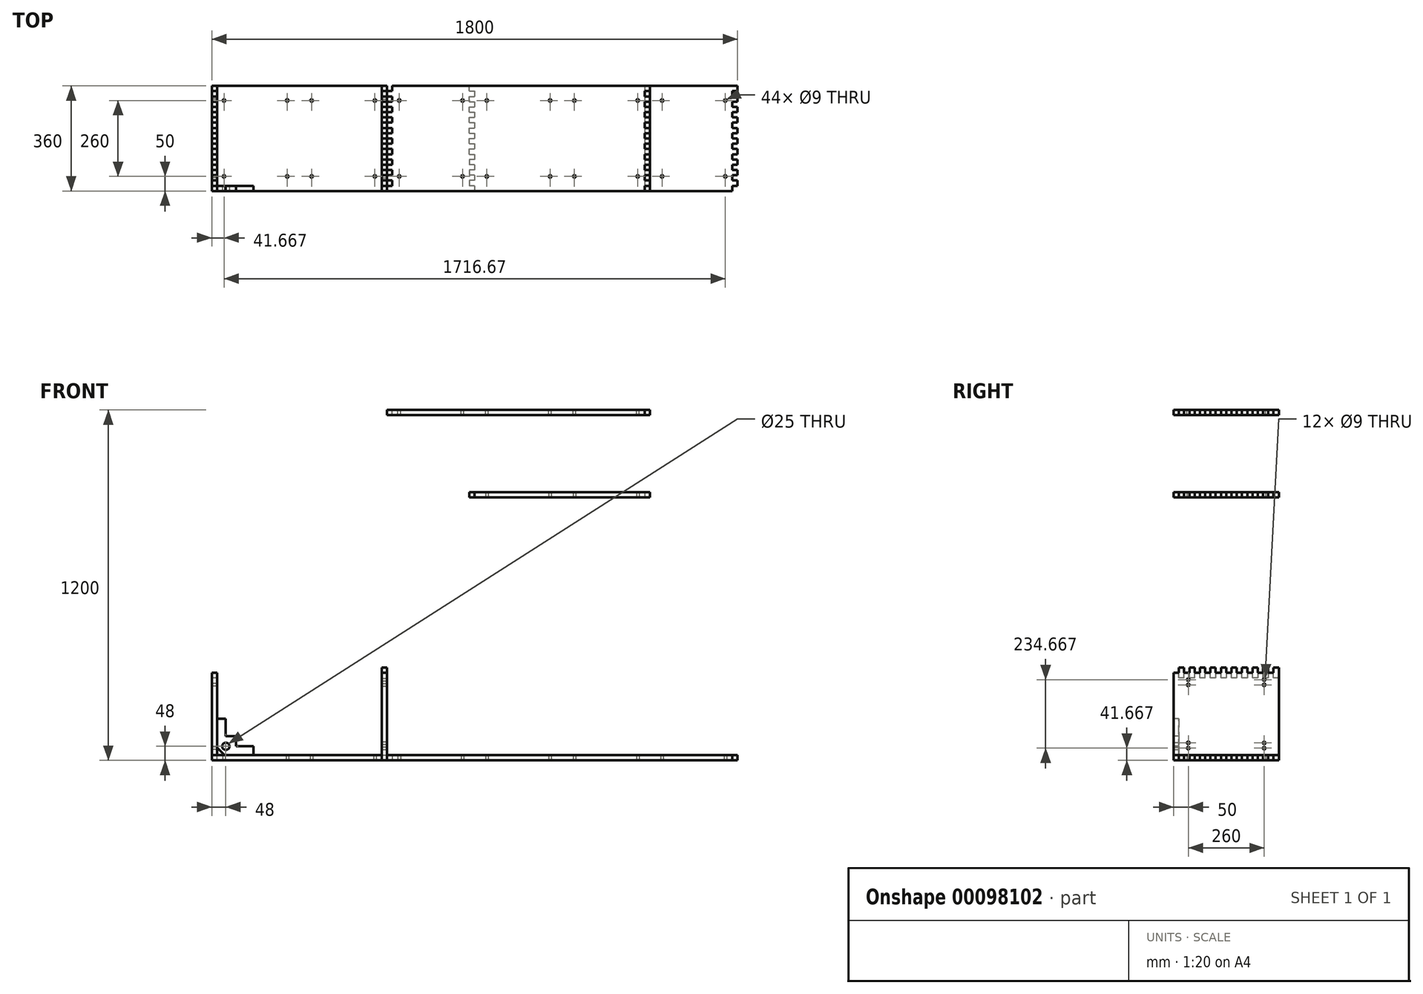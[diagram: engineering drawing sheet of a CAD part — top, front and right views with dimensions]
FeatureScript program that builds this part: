
annotation { "Feature Type Name" : "Feature", "Feature Type Description" : "" }
export const myFeature = defineFeature(function(context is Context, id is Id, definition is map)
    precondition{}
    {
        {
            var Q0;
            Q0=qCreatedBy(makeId("Right.planeOp"),FACE);
            cPlane(context, id + "F0", {"entities" : qUnion([Q0]), "cplaneType" : CPlaneType.OFFSET, "offset" : 300 * mm, "width" : 150 * mm, "height" : 150 * mm});
        }
        {
            var Q0;
            Q0=qCreatedBy(makeId("Right.planeOp"),FACE);
            cPlane(context, id + "F1", {"entities" : qUnion([Q0]), "cplaneType" : CPlaneType.OFFSET, "offset" : 600 * mm, "width" : 150 * mm, "height" : 150 * mm});
        }
        {
            var Q0;
            Q0=qCreatedBy(makeId("Right.planeOp"),FACE);
            cPlane(context, id + "F2", {"entities" : qUnion([Q0]), "cplaneType" : CPlaneType.OFFSET, "offset" : 900 * mm, "width" : 150 * mm, "height" : 150 * mm});
        }
        {
            var Q0;
            Q0=qCreatedBy(makeId("Right.planeOp"),FACE);
            cPlane(context, id + "F3", {"entities" : qUnion([Q0]), "cplaneType" : CPlaneType.OFFSET, "offset" : 1200 * mm, "width" : 150 * mm, "height" : 150 * mm});
        }
        {
            var Q0;
            Q0=qCreatedBy(makeId("Right.planeOp"),FACE);
            cPlane(context, id + "F4", {"entities" : qUnion([Q0]), "cplaneType" : CPlaneType.OFFSET, "offset" : 1500 * mm, "width" : 150 * mm, "height" : 150 * mm});
        }
        {
            var Q0;
            Q0=qCreatedBy(makeId("Right.planeOp"),FACE);
            cPlane(context, id + "F5", {"entities" : qUnion([Q0]), "cplaneType" : CPlaneType.OFFSET, "offset" : 1800 * mm, "width" : 150 * mm, "height" : 150 * mm});
        }
        {
            var Q0;
            Q0=qCreatedBy(makeId("Top.planeOp"),FACE);
            cPlane(context, id + "F6", {"entities" : qUnion([Q0]), "cplaneType" : CPlaneType.OFFSET, "offset" : 300 * mm, "width" : 150 * mm, "height" : 150 * mm});
        }
        {
            var Q0;
            Q0=qCreatedBy(makeId("Top.planeOp"),FACE);
            cPlane(context, id + "F7", {"entities" : qUnion([Q0]), "cplaneType" : CPlaneType.OFFSET, "offset" : 900 * mm, "width" : 150 * mm, "height" : 150 * mm});
        }
        {
            var Q0;
            Q0=qCreatedBy(makeId("Top.planeOp"),FACE);
            cPlane(context, id + "F8", {"entities" : qUnion([Q0]), "cplaneType" : CPlaneType.OFFSET, "offset" : 1200 * mm, "width" : 150 * mm, "height" : 150 * mm});
        }
        {
            var Q0;
            Q0=qCreatedBy(makeId("Front.planeOp"),FACE);
            cPlane(context, id + "F9", {"entities" : qUnion([Q0]), "cplaneType" : CPlaneType.OFFSET, "offset" : 360 * mm, "oppositeDirection" : true, "width" : 150 * mm, "height" : 150 * mm});
        }
        {
            var Q0;
            Q0=qCreatedBy(makeId("Top.planeOp"),FACE);
            var sketch = newSketch(context, id + "F10", { "sketchPlane" : qUnion([Q0])});
            skLineSegment(sketch, "E0.bottom", {"start": v(0, 0) * mm, "end": v(582, 0) * mm});
            skLineSegment(sketch, "E0.top", {"start": v(18, 360) * mm, "end": v(600, 360) * mm});
            skLineSegment(sketch, "E0.left", {"start": v(0, 0) * mm, "end": v(0, 18) * mm});
            skLineSegment(sketch, "E0.right", {"start": v(582, 0) * mm, "end": v(582, 18) * mm});
            skLineSegment(sketch, "E1.top", {"start": v(582, 0) * mm, "end": v(0, 0) * mm});
            skLineSegment(sketch, "E2.right", {"start": v(0, 0) * mm, "end": v(0, 0) * mm});
            skLineSegment(sketch, "E3", {"start": v(18, 18) * mm, "end": v(18, 36) * mm});
            skLineSegment(sketch, "E4", {"start": v(600, 18) * mm, "end": v(600, 36) * mm});
            skLineSegment(sketch, "E5", {"start": v(0, 342) * mm, "end": v(18, 342) * mm});
            skLineSegment(sketch, "E6", {"start": v(0, 36) * mm, "end": v(18, 36) * mm});
            skLineSegment(sketch, "E7", {"start": v(0, 54) * mm, "end": v(18, 54) * mm});
            skLineSegment(sketch, "E8", {"start": v(0, 324) * mm, "end": v(18, 324) * mm});
            skLineSegment(sketch, "E9.trimOffspring", {"start": v(18, 342) * mm, "end": v(18, 342) * mm});
            skLineSegment(sketch, "E10.trimOffspring", {"start": v(0, 324) * mm, "end": v(0, 342) * mm});
            skLineSegment(sketch, "E11.trimOffspring", {"start": v(18, 54) * mm, "end": v(18, 72) * mm});
            skLineSegment(sketch, "E12.trimOffspring", {"start": v(0, 36) * mm, "end": v(0, 54) * mm});
            skLineSegment(sketch, "E13.trimOffspring", {"start": v(582, 36) * mm, "end": v(582, 54) * mm});
            skLineSegment(sketch, "E14.trimOffspring", {"start": v(600, 54) * mm, "end": v(600, 72) * mm});
            skLineSegment(sketch, "E15.trimOffspring", {"start": v(582, 324) * mm, "end": v(600, 324) * mm});
            skLineSegment(sketch, "E16.trimOffspring", {"start": v(582, 54) * mm, "end": v(600, 54) * mm});
            skLineSegment(sketch, "E17.trimOffspring", {"start": v(582, 36) * mm, "end": v(600, 36) * mm});
            skLineSegment(sketch, "E18.trimOffspring", {"start": v(582, 18) * mm, "end": v(600, 18) * mm});
            skPoint(sketch, "E19", {"position": v(300, 360) * mm});
            skLineSegment(sketch, "E20", {"start": v(0, 0) * mm, "end": v(300, 360) * mm, "construction": true});
            skPoint(sketch, "E21", {"position": v(600, 0) * mm});
            skLineSegment(sketch, "E22", {"start": v(600, 0) * mm, "end": v(300, 360) * mm, "construction": true});
            skPoint(sketch, "E23", {"position": v(300, 0) * mm});
            skLineSegment(sketch, "E24", {"start": v(0, 360) * mm, "end": v(300, 0) * mm, "construction": true});
            skLineSegment(sketch, "E25", {"start": v(300.4, 0.5) * mm, "end": v(600, 360) * mm, "construction": true});
            skCircle(sketch, "E26", {"center": v(41.67, 50) * mm, "radius": 4.5 * mm});
            skCircle(sketch, "E27.MirrorC", {"center": v(558.33, 50) * mm, "radius": 4.5 * mm});
            skCircle(sketch, "E28", {"center": v(41.67, 310) * mm, "radius": 4.5 * mm});
            skCircle(sketch, "E29.MirrorC", {"center": v(558.33, 310) * mm, "radius": 4.5 * mm});
            skLineSegment(sketch, "E30", {"start": v(150, 180) * mm, "end": v(150, 216.14) * mm, "construction": true});
            skCircle(sketch, "E31.MirrorC", {"center": v(258.33, 50) * mm, "radius": 4.5 * mm});
            skCircle(sketch, "E32.MirrorC", {"center": v(258.33, 310) * mm, "radius": 4.5 * mm});
            skLineSegment(sketch, "E33", {"start": v(450, 180) * mm, "end": v(450, 216.39) * mm, "construction": true});
            skCircle(sketch, "E34.MirrorC", {"center": v(341.67, 310) * mm, "radius": 4.5 * mm});
            skCircle(sketch, "E35.MirrorC", {"center": v(341.67, 50) * mm, "radius": 4.5 * mm});
            skLineSegment(sketch, "E36", {"start": v(18, 72) * mm, "end": v(0, 72) * mm});
            skLineSegment(sketch, "E37", {"start": v(0, 72) * mm, "end": v(0, 90) * mm});
            skLineSegment(sketch, "E38", {"start": v(0, 90) * mm, "end": v(18, 90) * mm});
            skLineSegment(sketch, "E39", {"start": v(18, 108) * mm, "end": v(0, 108) * mm});
            skLineSegment(sketch, "E40", {"start": v(0, 108) * mm, "end": v(0, 126) * mm});
            skLineSegment(sketch, "E41", {"start": v(0, 126) * mm, "end": v(18, 126) * mm});
            skLineSegment(sketch, "E42", {"start": v(18, 144) * mm, "end": v(0, 144) * mm});
            skLineSegment(sketch, "E43", {"start": v(0, 144) * mm, "end": v(0, 162) * mm});
            skLineSegment(sketch, "E44", {"start": v(0, 162) * mm, "end": v(18, 162) * mm});
            skLineSegment(sketch, "E45", {"start": v(18, 180) * mm, "end": v(0, 180) * mm});
            skLineSegment(sketch, "E46", {"start": v(0, 180) * mm, "end": v(0, 198) * mm});
            skLineSegment(sketch, "E47", {"start": v(0, 198) * mm, "end": v(18, 198) * mm});
            skLineSegment(sketch, "E48", {"start": v(18, 216) * mm, "end": v(0, 216) * mm});
            skLineSegment(sketch, "E49", {"start": v(0, 216) * mm, "end": v(0, 234) * mm});
            skLineSegment(sketch, "E50", {"start": v(0, 234) * mm, "end": v(18, 234) * mm});
            skLineSegment(sketch, "E51.trimOffspring", {"start": v(18, 90) * mm, "end": v(18, 108) * mm});
            skLineSegment(sketch, "E52.trimOffspring", {"start": v(18, 162) * mm, "end": v(18, 180) * mm});
            skLineSegment(sketch, "E53.trimOffspring", {"start": v(18, 198) * mm, "end": v(18, 216) * mm});
            skLineSegment(sketch, "E54.trimOffspring", {"start": v(18, 234) * mm, "end": v(18, 252) * mm});
            skLineSegment(sketch, "E55", {"start": v(18, 252) * mm, "end": v(0, 252) * mm});
            skLineSegment(sketch, "E56", {"start": v(0, 252) * mm, "end": v(0, 270) * mm});
            skLineSegment(sketch, "E57", {"start": v(0, 270) * mm, "end": v(18, 270) * mm});
            skLineSegment(sketch, "E58", {"start": v(18, 288) * mm, "end": v(0, 288) * mm});
            skLineSegment(sketch, "E59", {"start": v(0, 288) * mm, "end": v(0, 306) * mm});
            skLineSegment(sketch, "E60", {"start": v(0, 306) * mm, "end": v(18, 306) * mm});
            skLineSegment(sketch, "E61", {"start": v(18, 126) * mm, "end": v(18, 144) * mm});
            skLineSegment(sketch, "E62", {"start": v(18, 342) * mm, "end": v(18, 360) * mm});
            skLineSegment(sketch, "E63", {"start": v(0, 342) * mm, "end": v(0, 360) * mm, "construction": true});
            skLineSegment(sketch, "E64.trimOffspring", {"start": v(18, 306) * mm, "end": v(18, 324) * mm});
            skLineSegment(sketch, "E65.trimOffspring", {"start": v(18, 270) * mm, "end": v(18, 288) * mm});
            skLineSegment(sketch, "E66", {"start": v(18, 18) * mm, "end": v(0, 18) * mm});
            skLineSegment(sketch, "E67", {"start": v(600, 72) * mm, "end": v(582, 72) * mm});
            skLineSegment(sketch, "E68", {"start": v(582, 72) * mm, "end": v(582, 90) * mm});
            skLineSegment(sketch, "E69", {"start": v(582, 90) * mm, "end": v(600, 90) * mm});
            skLineSegment(sketch, "E70", {"start": v(600, 108) * mm, "end": v(582, 108) * mm});
            skLineSegment(sketch, "E71", {"start": v(582, 108) * mm, "end": v(582, 126) * mm});
            skLineSegment(sketch, "E72", {"start": v(582, 126) * mm, "end": v(600, 126) * mm});
            skLineSegment(sketch, "E73", {"start": v(600, 144) * mm, "end": v(582, 144) * mm});
            skLineSegment(sketch, "E74", {"start": v(582, 144) * mm, "end": v(582, 162) * mm});
            skLineSegment(sketch, "E75", {"start": v(582, 162) * mm, "end": v(600, 162) * mm});
            skLineSegment(sketch, "E76.trimOffspring", {"start": v(600, 90) * mm, "end": v(600, 108) * mm});
            skLineSegment(sketch, "E77.trimOffspring", {"start": v(600, 126) * mm, "end": v(600, 144) * mm});
            skLineSegment(sketch, "E78.trimOffspring", {"start": v(600, 162) * mm, "end": v(600, 180) * mm});
            skLineSegment(sketch, "E79", {"start": v(600, 180) * mm, "end": v(582, 180) * mm});
            skLineSegment(sketch, "E80", {"start": v(582, 180) * mm, "end": v(582, 198) * mm});
            skLineSegment(sketch, "E81", {"start": v(582, 198) * mm, "end": v(600, 198) * mm});
            skLineSegment(sketch, "E82", {"start": v(600, 216) * mm, "end": v(582, 216) * mm});
            skLineSegment(sketch, "E83", {"start": v(582, 216) * mm, "end": v(582, 234) * mm});
            skLineSegment(sketch, "E84", {"start": v(582, 234) * mm, "end": v(600, 234) * mm});
            skLineSegment(sketch, "E85", {"start": v(582, 252) * mm, "end": v(582, 270) * mm});
            skLineSegment(sketch, "E86", {"start": v(582, 270) * mm, "end": v(600, 270) * mm});
            skLineSegment(sketch, "E87", {"start": v(600, 288) * mm, "end": v(582, 288) * mm});
            skLineSegment(sketch, "E88", {"start": v(582, 288) * mm, "end": v(582, 306) * mm});
            skLineSegment(sketch, "E89", {"start": v(582, 306) * mm, "end": v(600, 306) * mm});
            skLineSegment(sketch, "E90", {"start": v(582, 252) * mm, "end": v(600, 252) * mm});
            skLineSegment(sketch, "E91", {"start": v(582, 324) * mm, "end": v(582, 342) * mm});
            skLineSegment(sketch, "E92", {"start": v(582, 342) * mm, "end": v(600, 342) * mm});
            skLineSegment(sketch, "E93", {"start": v(600, 342) * mm, "end": v(600, 360) * mm});
            skLineSegment(sketch, "E94.trimOffspring", {"start": v(600, 306) * mm, "end": v(600, 324) * mm});
            skLineSegment(sketch, "E95.trimOffspring", {"start": v(600, 270) * mm, "end": v(600, 288) * mm});
            skLineSegment(sketch, "E96.trimOffspring", {"start": v(600, 234) * mm, "end": v(600, 252) * mm});
            skLineSegment(sketch, "E97.trimOffspring", {"start": v(600, 198) * mm, "end": v(600, 216) * mm});
            skSolve(sketch);
        }
        {
            var Q0;
            Q0 = qSketchRegion(id + "F10", true);
            extrude(context, id + "F11", {"entities" : qUnion([Q0]), "depth" : 18 * mm});
        }
        {
            var Q0;
            Q0=qCreatedBy(makeId("Top.planeOp"),FACE);
            var sketch = newSketch(context, id + "F12", { "sketchPlane" : qUnion([Q0])});
            skLineSegment(sketch, "E98.top", {"start": v(618, 360) * mm, "end": v(1800, 360) * mm});
            skLineSegment(sketch, "E98.left", {"start": v(600, 0) * mm, "end": v(600, 18) * mm});
            skLineSegment(sketch, "E98.right", {"start": v(1782, 0) * mm, "end": v(1782, 18) * mm});
            skLineSegment(sketch, "E99.top", {"start": v(1782, 0) * mm, "end": v(600, 0) * mm});
            skLineSegment(sketch, "E100.right", {"start": v(600, 0) * mm, "end": v(600, 0) * mm});
            skLineSegment(sketch, "E101", {"start": v(618, 18) * mm, "end": v(618, 36) * mm});
            skLineSegment(sketch, "E102", {"start": v(1800, 18) * mm, "end": v(1800, 36) * mm});
            skLineSegment(sketch, "E103", {"start": v(600, 342) * mm, "end": v(618, 342) * mm});
            skLineSegment(sketch, "E104.trimOffspring", {"start": v(1782, 342) * mm, "end": v(1800, 342) * mm});
            skLineSegment(sketch, "E105", {"start": v(600, 18) * mm, "end": v(618, 18) * mm});
            skLineSegment(sketch, "E106", {"start": v(600, 36) * mm, "end": v(618, 36) * mm});
            skLineSegment(sketch, "E107", {"start": v(600, 54) * mm, "end": v(618, 54) * mm});
            skLineSegment(sketch, "E108.trimOffspring", {"start": v(618, 342) * mm, "end": v(618, 360) * mm});
            skLineSegment(sketch, "E109.trimOffspring", {"start": v(618, 54) * mm, "end": v(618, 72) * mm});
            skLineSegment(sketch, "E110.trimOffspring", {"start": v(600, 36) * mm, "end": v(600, 54) * mm});
            skLineSegment(sketch, "E111.trimOffspring", {"start": v(1782, 36) * mm, "end": v(1782, 54) * mm});
            skLineSegment(sketch, "E112.trimOffspring", {"start": v(1800, 54) * mm, "end": v(1800, 72) * mm});
            skLineSegment(sketch, "E113.trimOffspring", {"start": v(1800, 342) * mm, "end": v(1800, 360) * mm});
            skLineSegment(sketch, "E114.trimOffspring", {"start": v(1782, 324) * mm, "end": v(1782, 342) * mm});
            skLineSegment(sketch, "E115.trimOffspring", {"start": v(1782, 324) * mm, "end": v(1800, 324) * mm});
            skLineSegment(sketch, "E116.trimOffspring", {"start": v(1782, 306) * mm, "end": v(1800, 306) * mm});
            skLineSegment(sketch, "E117.trimOffspring", {"start": v(1782, 54) * mm, "end": v(1800, 54) * mm});
            skLineSegment(sketch, "E118.trimOffspring", {"start": v(1782, 36) * mm, "end": v(1800, 36) * mm});
            skLineSegment(sketch, "E119.trimOffspring", {"start": v(1782, 18) * mm, "end": v(1800, 18) * mm});
            skLineSegment(sketch, "E120", {"start": v(600, 0) * mm, "end": v(900, 360) * mm, "construction": true});
            skLineSegment(sketch, "E121", {"start": v(600, 360) * mm, "end": v(900, 0) * mm, "construction": true});
            skLineSegment(sketch, "E122", {"start": v(750, 180) * mm, "end": v(694.2, 180) * mm, "construction": true});
            skLineSegment(sketch, "E123", {"start": v(750, 180) * mm, "end": v(750, 233.06) * mm, "construction": true});
            skCircle(sketch, "E124", {"center": v(858.33, 50) * mm, "radius": 4.5 * mm});
            skCircle(sketch, "E125.MirrorC", {"center": v(641.67, 50) * mm, "radius": 4.5 * mm});
            skCircle(sketch, "E126.MirrorC", {"center": v(941.67, 50) * mm, "radius": 4.5 * mm});
            skCircle(sketch, "E127.MirrorC", {"center": v(1158.33, 50) * mm, "radius": 4.5 * mm});
            skCircle(sketch, "E128.MirrorC", {"center": v(1241.67, 50) * mm, "radius": 4.5 * mm});
            skCircle(sketch, "E129.MirrorC", {"center": v(1458.33, 50) * mm, "radius": 4.5 * mm});
            skCircle(sketch, "E130.MirrorC", {"center": v(1541.67, 50) * mm, "radius": 4.5 * mm});
            skCircle(sketch, "E131.MirrorC", {"center": v(1758.33, 50) * mm, "radius": 4.5 * mm});
            skCircle(sketch, "E132.MirrorC", {"center": v(641.67, 310) * mm, "radius": 4.5 * mm});
            skCircle(sketch, "E133.MirrorC", {"center": v(858.33, 310) * mm, "radius": 4.5 * mm});
            skCircle(sketch, "E134.MirrorC", {"center": v(941.67, 310) * mm, "radius": 4.5 * mm});
            skCircle(sketch, "E135.MirrorC", {"center": v(1158.33, 310) * mm, "radius": 4.5 * mm});
            skCircle(sketch, "E136.MirrorC", {"center": v(1241.67, 310) * mm, "radius": 4.5 * mm});
            skCircle(sketch, "E137.MirrorC", {"center": v(1458.33, 310) * mm, "radius": 4.5 * mm});
            skCircle(sketch, "E138.MirrorC", {"center": v(1541.67, 310) * mm, "radius": 4.5 * mm});
            skCircle(sketch, "E139.MirrorC", {"center": v(1758.33, 310) * mm, "radius": 4.5 * mm});
            skLineSegment(sketch, "E140", {"start": v(618, 72) * mm, "end": v(600, 72) * mm});
            skLineSegment(sketch, "E141", {"start": v(600, 72) * mm, "end": v(600, 90) * mm});
            skLineSegment(sketch, "E142", {"start": v(600, 90) * mm, "end": v(618, 90) * mm});
            skLineSegment(sketch, "E143", {"start": v(618, 108) * mm, "end": v(600, 108) * mm});
            skLineSegment(sketch, "E144", {"start": v(600, 108) * mm, "end": v(600, 126) * mm});
            skLineSegment(sketch, "E145", {"start": v(600, 126) * mm, "end": v(618, 126) * mm});
            skLineSegment(sketch, "E146", {"start": v(618, 144) * mm, "end": v(600, 144) * mm});
            skLineSegment(sketch, "E147", {"start": v(600, 144) * mm, "end": v(600, 162) * mm});
            skLineSegment(sketch, "E148", {"start": v(600, 162) * mm, "end": v(618, 162) * mm});
            skLineSegment(sketch, "E149", {"start": v(618, 180) * mm, "end": v(600, 180) * mm});
            skLineSegment(sketch, "E150", {"start": v(600, 180) * mm, "end": v(600, 198) * mm});
            skLineSegment(sketch, "E151", {"start": v(600, 198) * mm, "end": v(618, 198) * mm});
            skLineSegment(sketch, "E152", {"start": v(618, 216) * mm, "end": v(600, 216) * mm});
            skLineSegment(sketch, "E153", {"start": v(600, 216) * mm, "end": v(600, 234) * mm});
            skLineSegment(sketch, "E154", {"start": v(600, 234) * mm, "end": v(618, 234) * mm});
            skLineSegment(sketch, "E155", {"start": v(618, 252) * mm, "end": v(600, 252) * mm});
            skLineSegment(sketch, "E156", {"start": v(600, 252) * mm, "end": v(600, 270) * mm});
            skLineSegment(sketch, "E157", {"start": v(600, 270) * mm, "end": v(618, 270) * mm});
            skLineSegment(sketch, "E158.trimOffspring", {"start": v(618, 90) * mm, "end": v(618, 108) * mm});
            skLineSegment(sketch, "E159.trimOffspring", {"start": v(618, 126) * mm, "end": v(618, 144) * mm});
            skLineSegment(sketch, "E160.trimOffspring", {"start": v(618, 162) * mm, "end": v(618, 180) * mm});
            skLineSegment(sketch, "E161.trimOffspring", {"start": v(618, 198) * mm, "end": v(618, 216) * mm});
            skLineSegment(sketch, "E162.trimOffspring", {"start": v(618, 234) * mm, "end": v(618, 252) * mm});
            skLineSegment(sketch, "E163", {"start": v(600, 342) * mm, "end": v(600, 324) * mm});
            skLineSegment(sketch, "E164", {"start": v(600, 324) * mm, "end": v(618, 324) * mm});
            skLineSegment(sketch, "E165", {"start": v(618, 324) * mm, "end": v(618, 306) * mm});
            skLineSegment(sketch, "E166", {"start": v(618, 306) * mm, "end": v(600, 306) * mm});
            skLineSegment(sketch, "E167", {"start": v(600, 306) * mm, "end": v(600, 288) * mm});
            skLineSegment(sketch, "E168", {"start": v(600, 288) * mm, "end": v(618, 288) * mm});
            skLineSegment(sketch, "E169", {"start": v(618, 288) * mm, "end": v(618, 270) * mm});
            skLineSegment(sketch, "E170", {"start": v(1800, 324) * mm, "end": v(1800, 306) * mm});
            skLineSegment(sketch, "E171", {"start": v(1800, 72) * mm, "end": v(1782, 72) * mm});
            skLineSegment(sketch, "E172", {"start": v(1782, 72) * mm, "end": v(1782, 90) * mm});
            skLineSegment(sketch, "E173", {"start": v(1782, 90) * mm, "end": v(1800, 90) * mm});
            skLineSegment(sketch, "E174", {"start": v(1800, 108) * mm, "end": v(1782, 108) * mm});
            skLineSegment(sketch, "E175", {"start": v(1782, 108) * mm, "end": v(1782, 126) * mm});
            skLineSegment(sketch, "E176", {"start": v(1782, 126) * mm, "end": v(1800, 126) * mm});
            skLineSegment(sketch, "E177", {"start": v(1800, 144) * mm, "end": v(1782, 144) * mm});
            skLineSegment(sketch, "E178", {"start": v(1782, 144) * mm, "end": v(1782, 162) * mm});
            skLineSegment(sketch, "E179", {"start": v(1782, 162) * mm, "end": v(1800, 162) * mm});
            skLineSegment(sketch, "E180", {"start": v(1800, 180) * mm, "end": v(1782, 180) * mm});
            skLineSegment(sketch, "E181", {"start": v(1782, 180) * mm, "end": v(1782, 198) * mm});
            skLineSegment(sketch, "E182", {"start": v(1782, 198) * mm, "end": v(1800, 198) * mm});
            skLineSegment(sketch, "E183", {"start": v(1800, 216) * mm, "end": v(1782, 216) * mm});
            skLineSegment(sketch, "E184", {"start": v(1782, 216) * mm, "end": v(1782, 234) * mm});
            skLineSegment(sketch, "E185", {"start": v(1782, 234) * mm, "end": v(1800, 234) * mm});
            skLineSegment(sketch, "E186", {"start": v(1800, 252) * mm, "end": v(1782, 252) * mm});
            skLineSegment(sketch, "E187", {"start": v(1782, 252) * mm, "end": v(1782, 270) * mm});
            skLineSegment(sketch, "E188", {"start": v(1782, 270) * mm, "end": v(1800, 270) * mm});
            skLineSegment(sketch, "E189", {"start": v(1800, 288) * mm, "end": v(1782, 288) * mm});
            skLineSegment(sketch, "E190", {"start": v(1782, 288) * mm, "end": v(1782, 306) * mm});
            skLineSegment(sketch, "E191.trimOffspring", {"start": v(1800, 90) * mm, "end": v(1800, 108) * mm});
            skLineSegment(sketch, "E192.trimOffspring", {"start": v(1800, 126) * mm, "end": v(1800, 144) * mm});
            skLineSegment(sketch, "E193.trimOffspring", {"start": v(1800, 162) * mm, "end": v(1800, 180) * mm});
            skLineSegment(sketch, "E194.trimOffspring", {"start": v(1800, 198) * mm, "end": v(1800, 216) * mm});
            skLineSegment(sketch, "E195.trimOffspring", {"start": v(1800, 234) * mm, "end": v(1800, 252) * mm});
            skLineSegment(sketch, "E196.trimOffspring", {"start": v(1800, 270) * mm, "end": v(1800, 288) * mm});
            skSolve(sketch);
        }
        {
            var Q0;
            Q0 = qSketchRegion(id + "F12", true);
            extrude(context, id + "F13", {"entities" : qUnion([Q0]), "depth" : 18 * mm});
        }
        {
            var Q0;
            Q0=qCreatedBy(makeId("Right.planeOp"),FACE);
            var sketch = newSketch(context, id + "F14", { "sketchPlane" : qUnion([Q0])});
            skLineSegment(sketch, "E197.bottom", {"start": v(360, 0) * mm, "end": v(360, 282) * mm});
            skLineSegment(sketch, "E197.top", {"start": v(0, 18) * mm, "end": v(0, 300) * mm});
            skLineSegment(sketch, "E197.left", {"start": v(342, 18) * mm, "end": v(324, 18) * mm});
            skLineSegment(sketch, "E197.right", {"start": v(342, 300) * mm, "end": v(324, 300) * mm});
            skLineSegment(sketch, "E198.right", {"start": v(360, 18) * mm, "end": v(360, 18) * mm});
            skLineSegment(sketch, "E199", {"start": v(108, 0) * mm, "end": v(90, 0) * mm});
            skLineSegment(sketch, "E200", {"start": v(108, 282) * mm, "end": v(90, 282) * mm});
            skLineSegment(sketch, "E201", {"start": v(18, 0) * mm, "end": v(18, 18) * mm});
            skLineSegment(sketch, "E202.trimOffspring", {"start": v(18, 282) * mm, "end": v(18, 300) * mm});
            skLineSegment(sketch, "E203", {"start": v(108, 0) * mm, "end": v(108, 18) * mm});
            skLineSegment(sketch, "E204", {"start": v(36, 0) * mm, "end": v(36, 18) * mm});
            skLineSegment(sketch, "E205", {"start": v(90, 0) * mm, "end": v(90, 18) * mm});
            skLineSegment(sketch, "E206", {"start": v(72, 0) * mm, "end": v(72, 18) * mm});
            skLineSegment(sketch, "E207", {"start": v(54, 0) * mm, "end": v(54, 18) * mm});
            skLineSegment(sketch, "E208.trimOffspring", {"start": v(18, 18) * mm, "end": v(0, 18) * mm});
            skLineSegment(sketch, "E209.trimOffspring", {"start": v(36, 0) * mm, "end": v(18, 0) * mm});
            skLineSegment(sketch, "E210.trimOffspring", {"start": v(54, 18) * mm, "end": v(36, 18) * mm});
            skLineSegment(sketch, "E211.trimOffspring", {"start": v(72, 0) * mm, "end": v(54, 0) * mm});
            skLineSegment(sketch, "E212.trimOffspring", {"start": v(72, 18) * mm, "end": v(90, 18) * mm});
            skLineSegment(sketch, "E213.trimOffspring", {"start": v(90, 300) * mm, "end": v(72, 300) * mm});
            skLineSegment(sketch, "E214.trimOffspring", {"start": v(72, 282) * mm, "end": v(54, 282) * mm});
            skLineSegment(sketch, "E215.trimOffspring", {"start": v(54, 300) * mm, "end": v(36, 300) * mm});
            skLineSegment(sketch, "E216.trimOffspring", {"start": v(36, 282) * mm, "end": v(18, 282) * mm});
            skLineSegment(sketch, "E217.trimOffspring", {"start": v(18, 300) * mm, "end": v(0, 300) * mm});
            skLineSegment(sketch, "E218.trimOffspring", {"start": v(36, 282) * mm, "end": v(36, 300) * mm});
            skLineSegment(sketch, "E219.trimOffspring", {"start": v(54, 282) * mm, "end": v(54, 300) * mm});
            skLineSegment(sketch, "E220.trimOffspring", {"start": v(72, 282) * mm, "end": v(72, 300) * mm});
            skLineSegment(sketch, "E221.trimOffspring", {"start": v(90, 282) * mm, "end": v(90, 300) * mm});
            skLineSegment(sketch, "E222.trimOffspring", {"start": v(108, 282) * mm, "end": v(108, 300) * mm});
            skLineSegment(sketch, "E223", {"start": v(0, 0) * mm, "end": v(360, 300) * mm, "construction": true});
            skLineSegment(sketch, "E224", {"start": v(360, 0) * mm, "end": v(0, 300) * mm, "construction": true});
            skCircle(sketch, "E225", {"center": v(50, 258.33) * mm, "radius": 4.5 * mm});
            skLineSegment(sketch, "E226", {"start": v(180, 150) * mm, "end": v(216.3, 150) * mm, "construction": true});
            skLineSegment(sketch, "E227", {"start": v(180, 150) * mm, "end": v(180, 196.76) * mm, "construction": true});
            skCircle(sketch, "E228.MirrorC", {"center": v(310, 258.33) * mm, "radius": 4.5 * mm});
            skCircle(sketch, "E229.MirrorC", {"center": v(310, 41.67) * mm, "radius": 4.5 * mm});
            skCircle(sketch, "E230.MirrorC", {"center": v(50, 41.67) * mm, "radius": 4.5 * mm});
            skLineSegment(sketch, "E231", {"start": v(126, 18) * mm, "end": v(126, 0) * mm});
            skLineSegment(sketch, "E232", {"start": v(126, 0) * mm, "end": v(144, 0) * mm});
            skLineSegment(sketch, "E233", {"start": v(144, 0) * mm, "end": v(144, 18) * mm});
            skLineSegment(sketch, "E234", {"start": v(162, 18) * mm, "end": v(162, 0) * mm});
            skLineSegment(sketch, "E235", {"start": v(162, 0) * mm, "end": v(180, 0) * mm});
            skLineSegment(sketch, "E236", {"start": v(180, 0) * mm, "end": v(180, 18) * mm});
            skLineSegment(sketch, "E237", {"start": v(198, 18) * mm, "end": v(198, 0) * mm});
            skLineSegment(sketch, "E238", {"start": v(198, 0) * mm, "end": v(216, 0) * mm});
            skLineSegment(sketch, "E239", {"start": v(216, 0) * mm, "end": v(216, 18) * mm});
            skLineSegment(sketch, "E240.trimOffspring", {"start": v(198, 18) * mm, "end": v(180, 18) * mm});
            skLineSegment(sketch, "E241.trimOffspring", {"start": v(162, 18) * mm, "end": v(144, 18) * mm});
            skLineSegment(sketch, "E242.trimOffspring", {"start": v(126, 18) * mm, "end": v(108, 18) * mm});
            skLineSegment(sketch, "E243", {"start": v(234, 18) * mm, "end": v(234, 0) * mm});
            skLineSegment(sketch, "E244", {"start": v(234, 0) * mm, "end": v(252, 0) * mm});
            skLineSegment(sketch, "E245", {"start": v(252, 0) * mm, "end": v(252, 18) * mm});
            skLineSegment(sketch, "E246", {"start": v(270, 18) * mm, "end": v(270, 0) * mm});
            skLineSegment(sketch, "E247", {"start": v(270, 0) * mm, "end": v(288, 0) * mm});
            skLineSegment(sketch, "E248", {"start": v(288, 0) * mm, "end": v(288, 18) * mm});
            skLineSegment(sketch, "E249", {"start": v(306, 18) * mm, "end": v(306, 0) * mm});
            skLineSegment(sketch, "E250", {"start": v(306, 0) * mm, "end": v(324, 0) * mm});
            skLineSegment(sketch, "E251", {"start": v(324, 0) * mm, "end": v(324, 18) * mm});
            skLineSegment(sketch, "E252", {"start": v(342, 18) * mm, "end": v(342, 0) * mm});
            skLineSegment(sketch, "E253", {"start": v(342, 0) * mm, "end": v(360, 0) * mm});
            skLineSegment(sketch, "E254.trimOffspring", {"start": v(306, 18) * mm, "end": v(216, 18) * mm});
            skLineSegment(sketch, "E255", {"start": v(360, 282) * mm, "end": v(342, 282) * mm});
            skLineSegment(sketch, "E256", {"start": v(342, 282) * mm, "end": v(342, 300) * mm});
            skLineSegment(sketch, "E257", {"start": v(324, 300) * mm, "end": v(324, 282) * mm});
            skLineSegment(sketch, "E258", {"start": v(324, 282) * mm, "end": v(306, 282) * mm});
            skLineSegment(sketch, "E259", {"start": v(306, 282) * mm, "end": v(306, 300) * mm});
            skLineSegment(sketch, "E260", {"start": v(288, 300) * mm, "end": v(288, 282) * mm});
            skLineSegment(sketch, "E261", {"start": v(288, 282) * mm, "end": v(270, 282) * mm});
            skLineSegment(sketch, "E262", {"start": v(270, 282) * mm, "end": v(270, 300) * mm});
            skLineSegment(sketch, "E263", {"start": v(252, 300) * mm, "end": v(252, 282) * mm});
            skLineSegment(sketch, "E264", {"start": v(252, 282) * mm, "end": v(234, 282) * mm});
            skLineSegment(sketch, "E265", {"start": v(234, 282) * mm, "end": v(234, 300) * mm});
            skLineSegment(sketch, "E266", {"start": v(216, 300) * mm, "end": v(216, 282) * mm});
            skLineSegment(sketch, "E267", {"start": v(216, 282) * mm, "end": v(198, 282) * mm});
            skLineSegment(sketch, "E268", {"start": v(198, 282) * mm, "end": v(198, 300) * mm});
            skLineSegment(sketch, "E269", {"start": v(180, 300) * mm, "end": v(180, 282) * mm});
            skLineSegment(sketch, "E270", {"start": v(180, 282) * mm, "end": v(162, 282) * mm});
            skLineSegment(sketch, "E271", {"start": v(162, 282) * mm, "end": v(162, 300) * mm});
            skLineSegment(sketch, "E272", {"start": v(144, 300) * mm, "end": v(144, 282) * mm});
            skLineSegment(sketch, "E273", {"start": v(144, 282) * mm, "end": v(126, 282) * mm});
            skLineSegment(sketch, "E274", {"start": v(126, 282) * mm, "end": v(126, 300) * mm});
            skLineSegment(sketch, "E275.trimOffspring", {"start": v(126, 300) * mm, "end": v(108, 300) * mm});
            skLineSegment(sketch, "E276.trimOffspring", {"start": v(162, 300) * mm, "end": v(144, 300) * mm});
            skLineSegment(sketch, "E277.trimOffspring", {"start": v(198, 300) * mm, "end": v(180, 300) * mm});
            skLineSegment(sketch, "E278.trimOffspring", {"start": v(234, 300) * mm, "end": v(216, 300) * mm});
            skLineSegment(sketch, "E279.trimOffspring", {"start": v(270, 300) * mm, "end": v(252, 300) * mm});
            skLineSegment(sketch, "E280.trimOffspring", {"start": v(306, 300) * mm, "end": v(288, 300) * mm});
            skSolve(sketch);
        }
        {
            var Q0;
            Q0 = qSketchRegion(id + "F14", true);
            extrude(context, id + "F15", {"entities" : qUnion([Q0]), "depth" : 18 * mm});
        }
        {
            var Q0;
            Q0=qCreatedBy(id+"F1.planeOp",FACE);
            var sketch = newSketch(context, id + "F16", { "sketchPlane" : qUnion([Q0])});
            skLineSegment(sketch, "E281.bottom", {"start": v(360, 18) * mm, "end": v(360, 318) * mm});
            skLineSegment(sketch, "E281.top", {"start": v(0, 0) * mm, "end": v(0, 300) * mm});
            skLineSegment(sketch, "E281.left", {"start": v(342, 0) * mm, "end": v(324, 0) * mm});
            skLineSegment(sketch, "E281.right", {"start": v(342, 300) * mm, "end": v(324, 300) * mm});
            skLineSegment(sketch, "E282", {"start": v(108, 18) * mm, "end": v(90, 18) * mm});
            skLineSegment(sketch, "E283", {"start": v(108, 318) * mm, "end": v(90, 318) * mm});
            skLineSegment(sketch, "E284", {"start": v(18, 0) * mm, "end": v(18, 18) * mm});
            skLineSegment(sketch, "E285.trimOffspring", {"start": v(18, 300) * mm, "end": v(18, 318) * mm});
            skLineSegment(sketch, "E286", {"start": v(108, 0) * mm, "end": v(108, 18) * mm});
            skLineSegment(sketch, "E287", {"start": v(36, 0) * mm, "end": v(36, 18) * mm});
            skLineSegment(sketch, "E288", {"start": v(90, 0) * mm, "end": v(90, 18) * mm});
            skLineSegment(sketch, "E289", {"start": v(72, 0) * mm, "end": v(72, 18) * mm});
            skLineSegment(sketch, "E290", {"start": v(54, 0) * mm, "end": v(54, 18) * mm});
            skLineSegment(sketch, "E291.trimOffspring", {"start": v(18, 0) * mm, "end": v(0, 0) * mm});
            skLineSegment(sketch, "E292.trimOffspring", {"start": v(36, 18) * mm, "end": v(18, 18) * mm});
            skLineSegment(sketch, "E293.trimOffspring", {"start": v(54, 0) * mm, "end": v(36, 0) * mm});
            skLineSegment(sketch, "E294.trimOffspring", {"start": v(72, 18) * mm, "end": v(54, 18) * mm});
            skLineSegment(sketch, "E295.trimOffspring", {"start": v(72, 0) * mm, "end": v(90, 0) * mm});
            skLineSegment(sketch, "E296.trimOffspring", {"start": v(90, 300) * mm, "end": v(72, 300) * mm});
            skLineSegment(sketch, "E297.trimOffspring", {"start": v(72, 318) * mm, "end": v(54, 318) * mm});
            skLineSegment(sketch, "E298.trimOffspring", {"start": v(54, 300) * mm, "end": v(36, 300) * mm});
            skLineSegment(sketch, "E299.trimOffspring", {"start": v(36, 318) * mm, "end": v(18, 318) * mm});
            skLineSegment(sketch, "E300.trimOffspring", {"start": v(18, 300) * mm, "end": v(0, 300) * mm});
            skLineSegment(sketch, "E301.trimOffspring", {"start": v(36, 300) * mm, "end": v(36, 318) * mm});
            skLineSegment(sketch, "E302.trimOffspring", {"start": v(54, 300) * mm, "end": v(54, 318) * mm});
            skLineSegment(sketch, "E303.trimOffspring", {"start": v(72, 300) * mm, "end": v(72, 318) * mm});
            skLineSegment(sketch, "E304.trimOffspring", {"start": v(90, 300) * mm, "end": v(90, 318) * mm});
            skLineSegment(sketch, "E305.trimOffspring", {"start": v(108, 300) * mm, "end": v(108, 318) * mm});
            skLineSegment(sketch, "E306", {"start": v(0, 0) * mm, "end": v(360, 300) * mm, "construction": true});
            skLineSegment(sketch, "E307", {"start": v(360, 0) * mm, "end": v(0, 300) * mm, "construction": true});
            skCircle(sketch, "E308", {"center": v(50, 258.33) * mm, "radius": 4.5 * mm});
            skLineSegment(sketch, "E309", {"start": v(180, 150) * mm, "end": v(180, 180.6) * mm, "construction": true});
            skLineSegment(sketch, "E310", {"start": v(180, 150) * mm, "end": v(221.23, 150) * mm, "construction": true});
            skCircle(sketch, "E311.MirrorC", {"center": v(310, 258.33) * mm, "radius": 4.5 * mm});
            skCircle(sketch, "E312.MirrorC", {"center": v(310, 41.67) * mm, "radius": 4.5 * mm});
            skCircle(sketch, "E313.MirrorC", {"center": v(50, 41.67) * mm, "radius": 4.5 * mm});
            skCircle(sketch, "E314", {"center": v(50, 276.33) * mm, "radius": 4.5 * mm});
            skLineSegment(sketch, "E315", {"start": v(50, 258.33) * mm, "end": v(50, 276.33) * mm, "construction": true});
            skCircle(sketch, "E316", {"center": v(50, 59.67) * mm, "radius": 4.5 * mm});
            skLineSegment(sketch, "E317", {"start": v(50, 41.67) * mm, "end": v(50, 59.67) * mm, "construction": true});
            skCircle(sketch, "E318.MirrorC", {"center": v(310, 59.67) * mm, "radius": 4.5 * mm});
            skCircle(sketch, "E319.MirrorC", {"center": v(310, 276.33) * mm, "radius": 4.5 * mm});
            skLineSegment(sketch, "E320", {"start": v(162, 18) * mm, "end": v(180, 18) * mm});
            skLineSegment(sketch, "E321", {"start": v(126, 18) * mm, "end": v(126, 0) * mm});
            skLineSegment(sketch, "E322", {"start": v(144, 18) * mm, "end": v(144, 0) * mm});
            skLineSegment(sketch, "E323", {"start": v(162, 18) * mm, "end": v(162, 0) * mm});
            skLineSegment(sketch, "E324", {"start": v(180, 18) * mm, "end": v(180, 0) * mm});
            skLineSegment(sketch, "E325", {"start": v(198, 18) * mm, "end": v(198, 0) * mm});
            skLineSegment(sketch, "E326", {"start": v(216, 18) * mm, "end": v(216, 0) * mm});
            skLineSegment(sketch, "E327", {"start": v(234, 18) * mm, "end": v(234, 0) * mm});
            skLineSegment(sketch, "E328", {"start": v(252, 18) * mm, "end": v(252, 0) * mm});
            skLineSegment(sketch, "E329", {"start": v(270, 18) * mm, "end": v(270, 0) * mm});
            skLineSegment(sketch, "E330", {"start": v(288, 18) * mm, "end": v(288, 0) * mm});
            skLineSegment(sketch, "E331", {"start": v(306, 18) * mm, "end": v(306, 0) * mm});
            skLineSegment(sketch, "E332", {"start": v(324, 18) * mm, "end": v(324, 0) * mm});
            skLineSegment(sketch, "E333", {"start": v(342, 18) * mm, "end": v(342, 0) * mm});
            skLineSegment(sketch, "E334", {"start": v(144, 18) * mm, "end": v(126, 18) * mm});
            skLineSegment(sketch, "E335.trimOffspring", {"start": v(126, 0) * mm, "end": v(108, 0) * mm});
            skLineSegment(sketch, "E336.trimOffspring", {"start": v(162, 0) * mm, "end": v(144, 0) * mm});
            skLineSegment(sketch, "E337.trimOffspring", {"start": v(198, 18) * mm, "end": v(216, 18) * mm});
            skLineSegment(sketch, "E338.trimOffspring", {"start": v(198, 0) * mm, "end": v(180, 0) * mm});
            skLineSegment(sketch, "E339.trimOffspring", {"start": v(234, 18) * mm, "end": v(252, 18) * mm});
            skLineSegment(sketch, "E340.trimOffspring", {"start": v(234, 0) * mm, "end": v(216, 0) * mm});
            skLineSegment(sketch, "E341.trimOffspring", {"start": v(270, 18) * mm, "end": v(288, 18) * mm});
            skLineSegment(sketch, "E342.trimOffspring", {"start": v(270, 0) * mm, "end": v(252, 0) * mm});
            skLineSegment(sketch, "E343.trimOffspring", {"start": v(306, 18) * mm, "end": v(324, 18) * mm});
            skLineSegment(sketch, "E344.trimOffspring", {"start": v(306, 0) * mm, "end": v(288, 0) * mm});
            skLineSegment(sketch, "E345.trimOffspring", {"start": v(342, 18) * mm, "end": v(360, 18) * mm});
            skLineSegment(sketch, "E346", {"start": v(126, 318) * mm, "end": v(144, 318) * mm});
            skLineSegment(sketch, "E347", {"start": v(126, 318) * mm, "end": v(126, 300) * mm});
            skLineSegment(sketch, "E348", {"start": v(144, 318) * mm, "end": v(144, 300) * mm});
            skLineSegment(sketch, "E349", {"start": v(162, 318) * mm, "end": v(162, 300) * mm});
            skLineSegment(sketch, "E350", {"start": v(180, 318) * mm, "end": v(180, 300) * mm});
            skLineSegment(sketch, "E351", {"start": v(198, 318) * mm, "end": v(198, 300) * mm});
            skLineSegment(sketch, "E352", {"start": v(252, 318) * mm, "end": v(252, 300) * mm});
            skLineSegment(sketch, "E353", {"start": v(234, 318) * mm, "end": v(234, 300) * mm});
            skLineSegment(sketch, "E354", {"start": v(288, 318) * mm, "end": v(288, 300) * mm});
            skLineSegment(sketch, "E355", {"start": v(306, 318) * mm, "end": v(306, 300) * mm});
            skLineSegment(sketch, "E356", {"start": v(324, 318) * mm, "end": v(324, 300) * mm});
            skLineSegment(sketch, "E357", {"start": v(342, 318) * mm, "end": v(342, 300) * mm});
            skLineSegment(sketch, "E358", {"start": v(216, 318) * mm, "end": v(216, 300) * mm});
            skLineSegment(sketch, "E359", {"start": v(270, 318) * mm, "end": v(270, 300) * mm});
            skLineSegment(sketch, "E360.trimOffspring", {"start": v(126, 300) * mm, "end": v(108, 300) * mm});
            skLineSegment(sketch, "E361.trimOffspring", {"start": v(162, 318) * mm, "end": v(180, 318) * mm});
            skLineSegment(sketch, "E362.trimOffspring", {"start": v(162, 300) * mm, "end": v(144, 300) * mm});
            skLineSegment(sketch, "E363.trimOffspring", {"start": v(198, 318) * mm, "end": v(216, 318) * mm});
            skLineSegment(sketch, "E364.trimOffspring", {"start": v(198, 300) * mm, "end": v(180, 300) * mm});
            skLineSegment(sketch, "E365.trimOffspring", {"start": v(234, 318) * mm, "end": v(252, 318) * mm});
            skLineSegment(sketch, "E366.trimOffspring", {"start": v(234, 300) * mm, "end": v(216, 300) * mm});
            skLineSegment(sketch, "E367.trimOffspring", {"start": v(270, 318) * mm, "end": v(288, 318) * mm});
            skLineSegment(sketch, "E368.trimOffspring", {"start": v(270, 300) * mm, "end": v(252, 300) * mm});
            skLineSegment(sketch, "E369.trimOffspring", {"start": v(306, 318) * mm, "end": v(324, 318) * mm});
            skLineSegment(sketch, "E370.trimOffspring", {"start": v(306, 300) * mm, "end": v(288, 300) * mm});
            skLineSegment(sketch, "E371.trimOffspring", {"start": v(342, 318) * mm, "end": v(360, 318) * mm});
            skSolve(sketch);
        }
        {
            var Q0;
            Q0 = qSketchRegion(id + "F16", true);
            extrude(context, id + "F17", {"entities" : qUnion([Q0]), "oppositeDirection" : true, "depth" : 18 * mm});
        }
        {
            var Q0;
            Q0=qCreatedBy(id+"F8.planeOp",FACE);
            var sketch = newSketch(context, id + "F18", { "sketchPlane" : qUnion([Q0])});
            skLineSegment(sketch, "E372.bottom", {"start": v(1500, 360) * mm, "end": v(618, 360) * mm});
            skLineSegment(sketch, "E372.top", {"start": v(1482, 0) * mm, "end": v(600, 0) * mm});
            skLineSegment(sketch, "E372.left", {"start": v(1482, 342) * mm, "end": v(1482, 324) * mm});
            skLineSegment(sketch, "E372.right", {"start": v(600, 342) * mm, "end": v(600, 324) * mm});
            skLineSegment(sketch, "E373", {"start": v(1500, 108) * mm, "end": v(1500, 90) * mm});
            skLineSegment(sketch, "E374", {"start": v(618, 108) * mm, "end": v(618, 90) * mm});
            skLineSegment(sketch, "E375", {"start": v(1500, 18) * mm, "end": v(1482, 18) * mm});
            skLineSegment(sketch, "E376.trimOffspring", {"start": v(618, 18) * mm, "end": v(600, 18) * mm});
            skLineSegment(sketch, "E377", {"start": v(1500, 108) * mm, "end": v(1482, 108) * mm});
            skLineSegment(sketch, "E378", {"start": v(1500, 36) * mm, "end": v(1482, 36) * mm});
            skLineSegment(sketch, "E379", {"start": v(1500, 90) * mm, "end": v(1482, 90) * mm});
            skLineSegment(sketch, "E380", {"start": v(1500, 72) * mm, "end": v(1482, 72) * mm});
            skLineSegment(sketch, "E381", {"start": v(1500, 54) * mm, "end": v(1482, 54) * mm});
            skLineSegment(sketch, "E382.trimOffspring", {"start": v(1482, 18) * mm, "end": v(1482, 0) * mm});
            skLineSegment(sketch, "E383.trimOffspring", {"start": v(1500, 36) * mm, "end": v(1500, 18) * mm});
            skLineSegment(sketch, "E384.trimOffspring", {"start": v(1482, 54) * mm, "end": v(1482, 36) * mm});
            skLineSegment(sketch, "E385.trimOffspring", {"start": v(1500, 72) * mm, "end": v(1500, 54) * mm});
            skLineSegment(sketch, "E386.trimOffspring", {"start": v(1482, 72) * mm, "end": v(1482, 90) * mm});
            skLineSegment(sketch, "E387.trimOffspring", {"start": v(600, 90) * mm, "end": v(600, 72) * mm});
            skLineSegment(sketch, "E388.trimOffspring", {"start": v(618, 72) * mm, "end": v(618, 54) * mm});
            skLineSegment(sketch, "E389.trimOffspring", {"start": v(600, 54) * mm, "end": v(600, 36) * mm});
            skLineSegment(sketch, "E390.trimOffspring", {"start": v(618, 36) * mm, "end": v(618, 18) * mm});
            skLineSegment(sketch, "E391.trimOffspring", {"start": v(600, 18) * mm, "end": v(600, 0) * mm});
            skLineSegment(sketch, "E392.trimOffspring", {"start": v(618, 36) * mm, "end": v(600, 36) * mm});
            skLineSegment(sketch, "E393.trimOffspring", {"start": v(618, 54) * mm, "end": v(600, 54) * mm});
            skLineSegment(sketch, "E394.trimOffspring", {"start": v(618, 72) * mm, "end": v(600, 72) * mm});
            skLineSegment(sketch, "E395.trimOffspring", {"start": v(618, 90) * mm, "end": v(600, 90) * mm});
            skLineSegment(sketch, "E396.trimOffspring", {"start": v(618, 108) * mm, "end": v(600, 108) * mm});
            skLineSegment(sketch, "E397", {"start": v(600, 0) * mm, "end": v(900, 360) * mm, "construction": true});
            skLineSegment(sketch, "E398", {"start": v(600, 360) * mm, "end": v(900, 0) * mm, "construction": true});
            skLineSegment(sketch, "E399", {"start": v(750, 180) * mm, "end": v(796.7, 180) * mm, "construction": true});
            skLineSegment(sketch, "E400", {"start": v(750, 180) * mm, "end": v(750, 236.32) * mm, "construction": true});
            skCircle(sketch, "E401", {"center": v(641.67, 50) * mm, "radius": 4.5 * mm});
            skCircle(sketch, "E402.MirrorC", {"center": v(858.33, 50) * mm, "radius": 4.5 * mm});
            skCircle(sketch, "E403.MirrorC", {"center": v(941.67, 50) * mm, "radius": 4.5 * mm});
            skCircle(sketch, "E404.MirrorC", {"center": v(1158.33, 50) * mm, "radius": 4.5 * mm});
            skCircle(sketch, "E405.MirrorC", {"center": v(1241.67, 50) * mm, "radius": 4.5 * mm});
            skCircle(sketch, "E406.MirrorC", {"center": v(1458.33, 50) * mm, "radius": 4.5 * mm});
            skCircle(sketch, "E407.MirrorC", {"center": v(641.67, 310) * mm, "radius": 4.5 * mm});
            skCircle(sketch, "E408.MirrorC", {"center": v(858.33, 310) * mm, "radius": 4.5 * mm});
            skCircle(sketch, "E409.MirrorC", {"center": v(941.67, 310) * mm, "radius": 4.5 * mm});
            skCircle(sketch, "E410.MirrorC", {"center": v(1158.33, 310) * mm, "radius": 4.5 * mm});
            skCircle(sketch, "E411.MirrorC", {"center": v(1241.67, 310) * mm, "radius": 4.5 * mm});
            skCircle(sketch, "E412.MirrorC", {"center": v(1458.33, 310) * mm, "radius": 4.5 * mm});
            skLineSegment(sketch, "E413", {"start": v(618, 126) * mm, "end": v(618, 144) * mm});
            skLineSegment(sketch, "E414", {"start": v(618, 126) * mm, "end": v(600, 126) * mm});
            skLineSegment(sketch, "E415", {"start": v(618, 144) * mm, "end": v(600, 144) * mm});
            skLineSegment(sketch, "E416", {"start": v(600, 162) * mm, "end": v(618, 162) * mm});
            skLineSegment(sketch, "E417", {"start": v(600, 180) * mm, "end": v(618, 180) * mm});
            skLineSegment(sketch, "E418", {"start": v(600, 198) * mm, "end": v(618, 198) * mm});
            skLineSegment(sketch, "E419", {"start": v(600, 216) * mm, "end": v(618, 216) * mm});
            skLineSegment(sketch, "E420", {"start": v(600, 234) * mm, "end": v(618, 234) * mm});
            skLineSegment(sketch, "E421", {"start": v(600, 252) * mm, "end": v(618, 252) * mm});
            skLineSegment(sketch, "E422", {"start": v(600, 270) * mm, "end": v(618, 270) * mm});
            skLineSegment(sketch, "E423", {"start": v(618, 288) * mm, "end": v(600, 288) * mm});
            skLineSegment(sketch, "E424", {"start": v(600, 306) * mm, "end": v(618, 306) * mm});
            skLineSegment(sketch, "E425", {"start": v(600, 324) * mm, "end": v(618, 324) * mm});
            skLineSegment(sketch, "E426", {"start": v(618, 342) * mm, "end": v(600, 342) * mm});
            skLineSegment(sketch, "E427.trimOffspring", {"start": v(600, 126) * mm, "end": v(600, 108) * mm});
            skLineSegment(sketch, "E428.trimOffspring", {"start": v(618, 162) * mm, "end": v(618, 180) * mm});
            skLineSegment(sketch, "E429.trimOffspring", {"start": v(600, 162) * mm, "end": v(600, 144) * mm});
            skLineSegment(sketch, "E430.trimOffspring", {"start": v(618, 198) * mm, "end": v(618, 216) * mm});
            skLineSegment(sketch, "E431.trimOffspring", {"start": v(600, 198) * mm, "end": v(600, 180) * mm});
            skLineSegment(sketch, "E432.trimOffspring", {"start": v(618, 234) * mm, "end": v(618, 252) * mm});
            skLineSegment(sketch, "E433.trimOffspring", {"start": v(600, 234) * mm, "end": v(600, 216) * mm});
            skLineSegment(sketch, "E434.trimOffspring", {"start": v(618, 270) * mm, "end": v(618, 288) * mm});
            skLineSegment(sketch, "E435.trimOffspring", {"start": v(600, 270) * mm, "end": v(600, 252) * mm});
            skLineSegment(sketch, "E436.trimOffspring", {"start": v(618, 306) * mm, "end": v(618, 324) * mm});
            skLineSegment(sketch, "E437.trimOffspring", {"start": v(600, 306) * mm, "end": v(600, 288) * mm});
            skLineSegment(sketch, "E438.trimOffspring", {"start": v(618, 342) * mm, "end": v(618, 360) * mm});
            skLineSegment(sketch, "E439", {"start": v(1500, 126) * mm, "end": v(1500, 144) * mm});
            skLineSegment(sketch, "E440", {"start": v(1482, 126) * mm, "end": v(1500, 126) * mm});
            skLineSegment(sketch, "E441", {"start": v(1482, 144) * mm, "end": v(1500, 144) * mm});
            skLineSegment(sketch, "E442", {"start": v(1482, 180) * mm, "end": v(1500, 180) * mm});
            skLineSegment(sketch, "E443", {"start": v(1482, 198) * mm, "end": v(1500, 198) * mm});
            skLineSegment(sketch, "E444", {"start": v(1482, 216) * mm, "end": v(1500, 216) * mm});
            skLineSegment(sketch, "E445", {"start": v(1482, 234) * mm, "end": v(1500, 234) * mm});
            skLineSegment(sketch, "E446", {"start": v(1482, 252) * mm, "end": v(1500, 252) * mm});
            skLineSegment(sketch, "E447", {"start": v(1482, 270) * mm, "end": v(1500, 270) * mm});
            skLineSegment(sketch, "E448", {"start": v(1482, 288) * mm, "end": v(1500, 288) * mm});
            skLineSegment(sketch, "E449", {"start": v(1482, 306) * mm, "end": v(1500, 306) * mm});
            skLineSegment(sketch, "E450", {"start": v(1482, 324) * mm, "end": v(1500, 324) * mm});
            skLineSegment(sketch, "E451", {"start": v(1482, 342) * mm, "end": v(1500, 342) * mm});
            skLineSegment(sketch, "E452", {"start": v(1482, 162) * mm, "end": v(1500, 162) * mm});
            skLineSegment(sketch, "E453.trimOffspring", {"start": v(1482, 126) * mm, "end": v(1482, 108) * mm});
            skLineSegment(sketch, "E454.trimOffspring", {"start": v(1500, 162) * mm, "end": v(1500, 180) * mm});
            skLineSegment(sketch, "E455.trimOffspring", {"start": v(1482, 162) * mm, "end": v(1482, 144) * mm});
            skLineSegment(sketch, "E456.trimOffspring", {"start": v(1500, 198) * mm, "end": v(1500, 216) * mm});
            skLineSegment(sketch, "E457.trimOffspring", {"start": v(1482, 198) * mm, "end": v(1482, 180) * mm});
            skLineSegment(sketch, "E458.trimOffspring", {"start": v(1500, 234) * mm, "end": v(1500, 252) * mm});
            skLineSegment(sketch, "E459.trimOffspring", {"start": v(1482, 234) * mm, "end": v(1482, 216) * mm});
            skLineSegment(sketch, "E460.trimOffspring", {"start": v(1500, 270) * mm, "end": v(1500, 288) * mm});
            skLineSegment(sketch, "E461.trimOffspring", {"start": v(1482, 270) * mm, "end": v(1482, 252) * mm});
            skLineSegment(sketch, "E462.trimOffspring", {"start": v(1500, 306) * mm, "end": v(1500, 324) * mm});
            skLineSegment(sketch, "E463.trimOffspring", {"start": v(1482, 306) * mm, "end": v(1482, 288) * mm});
            skLineSegment(sketch, "E464.trimOffspring", {"start": v(1500, 342) * mm, "end": v(1500, 360) * mm});
            skSolve(sketch);
        }
        {
            var Q0;
            Q0 = qSketchRegion(id + "F18", true);
            extrude(context, id + "F19", {"entities" : qUnion([Q0]), "oppositeDirection" : true, "depth" : 18 * mm});
        }
        {
            var Q0;
            Q0=qCreatedBy(id+"F7.planeOp",FACE);
            var sketch = newSketch(context, id + "F20", { "sketchPlane" : qUnion([Q0])});
            skLineSegment(sketch, "E465.bottom", {"start": v(1482, 360) * mm, "end": v(882, 360) * mm});
            skLineSegment(sketch, "E465.top", {"start": v(1500, 0) * mm, "end": v(900, 0) * mm});
            skLineSegment(sketch, "E465.left", {"start": v(1500, 342) * mm, "end": v(1500, 324) * mm});
            skLineSegment(sketch, "E465.right", {"start": v(900, 342) * mm, "end": v(900, 324) * mm});
            skLineSegment(sketch, "E466", {"start": v(1482, 108) * mm, "end": v(1482, 90) * mm});
            skLineSegment(sketch, "E467", {"start": v(882, 108) * mm, "end": v(882, 90) * mm});
            skLineSegment(sketch, "E468", {"start": v(1500, 18) * mm, "end": v(1482, 18) * mm});
            skLineSegment(sketch, "E469.trimOffspring", {"start": v(900, 18) * mm, "end": v(882, 18) * mm});
            skLineSegment(sketch, "E470", {"start": v(1500, 108) * mm, "end": v(1482, 108) * mm});
            skLineSegment(sketch, "E471", {"start": v(1500, 36) * mm, "end": v(1482, 36) * mm});
            skLineSegment(sketch, "E472", {"start": v(1500, 90) * mm, "end": v(1482, 90) * mm});
            skLineSegment(sketch, "E473", {"start": v(1500, 72) * mm, "end": v(1482, 72) * mm});
            skLineSegment(sketch, "E474", {"start": v(1500, 54) * mm, "end": v(1482, 54) * mm});
            skLineSegment(sketch, "E475.trimOffspring", {"start": v(1500, 18) * mm, "end": v(1500, 0) * mm});
            skLineSegment(sketch, "E476.trimOffspring", {"start": v(1482, 36) * mm, "end": v(1482, 18) * mm});
            skLineSegment(sketch, "E477.trimOffspring", {"start": v(1500, 54) * mm, "end": v(1500, 36) * mm});
            skLineSegment(sketch, "E478.trimOffspring", {"start": v(1482, 72) * mm, "end": v(1482, 54) * mm});
            skLineSegment(sketch, "E479.trimOffspring", {"start": v(1500, 72) * mm, "end": v(1500, 90) * mm});
            skLineSegment(sketch, "E480.trimOffspring", {"start": v(900, 90) * mm, "end": v(900, 72) * mm});
            skLineSegment(sketch, "E481.trimOffspring", {"start": v(882, 72) * mm, "end": v(882, 54) * mm});
            skLineSegment(sketch, "E482.trimOffspring", {"start": v(900, 54) * mm, "end": v(900, 36) * mm});
            skLineSegment(sketch, "E483.trimOffspring", {"start": v(882, 36) * mm, "end": v(882, 18) * mm});
            skLineSegment(sketch, "E484.trimOffspring", {"start": v(900, 18) * mm, "end": v(900, 0) * mm});
            skLineSegment(sketch, "E485.trimOffspring", {"start": v(900, 36) * mm, "end": v(882, 36) * mm});
            skLineSegment(sketch, "E486.trimOffspring", {"start": v(900, 54) * mm, "end": v(882, 54) * mm});
            skLineSegment(sketch, "E487.trimOffspring", {"start": v(900, 72) * mm, "end": v(882, 72) * mm});
            skLineSegment(sketch, "E488.trimOffspring", {"start": v(900, 90) * mm, "end": v(882, 90) * mm});
            skLineSegment(sketch, "E489.trimOffspring", {"start": v(900, 108) * mm, "end": v(882, 108) * mm});
            skLineSegment(sketch, "E490", {"start": v(900, 0) * mm, "end": v(1200, 360) * mm, "construction": true});
            skLineSegment(sketch, "E491", {"start": v(1500, 0) * mm, "end": v(1200, 360) * mm, "construction": true});
            skLineSegment(sketch, "E492", {"start": v(900, 360) * mm, "end": v(1200, 0) * mm, "construction": true});
            skLineSegment(sketch, "E493", {"start": v(1200, 0) * mm, "end": v(1500, 360) * mm, "construction": true});
            skCircle(sketch, "E494", {"center": v(941.67, 50) * mm, "radius": 4.5 * mm});
            skLineSegment(sketch, "E495", {"start": v(1050, 180) * mm, "end": v(1107.91, 180) * mm, "construction": true});
            skLineSegment(sketch, "E496", {"start": v(1050, 180) * mm, "end": v(1050, 221.23) * mm, "construction": true});
            skCircle(sketch, "E497.MirrorC", {"center": v(1158.33, 50) * mm, "radius": 4.5 * mm});
            skCircle(sketch, "E498.MirrorC", {"center": v(1458.33, 50) * mm, "radius": 4.5 * mm});
            skCircle(sketch, "E499.MirrorC", {"center": v(1241.67, 50) * mm, "radius": 4.5 * mm});
            skCircle(sketch, "E500.MirrorC", {"center": v(1458.33, 310) * mm, "radius": 4.5 * mm});
            skCircle(sketch, "E501.MirrorC", {"center": v(1241.67, 310) * mm, "radius": 4.5 * mm});
            skCircle(sketch, "E502.MirrorC", {"center": v(1158.33, 310) * mm, "radius": 4.5 * mm});
            skCircle(sketch, "E503.MirrorC", {"center": v(941.67, 310) * mm, "radius": 4.5 * mm});
            skLineSegment(sketch, "E504", {"start": v(882, 126) * mm, "end": v(882, 144) * mm});
            skLineSegment(sketch, "E505", {"start": v(882, 126) * mm, "end": v(900, 126) * mm});
            skLineSegment(sketch, "E506", {"start": v(882, 144) * mm, "end": v(900, 144) * mm});
            skLineSegment(sketch, "E507", {"start": v(882, 162) * mm, "end": v(900, 162) * mm});
            skLineSegment(sketch, "E508", {"start": v(882, 180) * mm, "end": v(900, 180) * mm});
            skLineSegment(sketch, "E509", {"start": v(882, 198) * mm, "end": v(900, 198) * mm});
            skLineSegment(sketch, "E510", {"start": v(882, 216) * mm, "end": v(900, 216) * mm});
            skLineSegment(sketch, "E511", {"start": v(882, 234) * mm, "end": v(900, 234) * mm});
            skLineSegment(sketch, "E512", {"start": v(882, 252) * mm, "end": v(900, 252) * mm});
            skLineSegment(sketch, "E513", {"start": v(882, 270) * mm, "end": v(900, 270) * mm});
            skLineSegment(sketch, "E514", {"start": v(882, 288) * mm, "end": v(900, 288) * mm});
            skLineSegment(sketch, "E515", {"start": v(882, 306) * mm, "end": v(900, 306) * mm});
            skLineSegment(sketch, "E516", {"start": v(882, 324) * mm, "end": v(900, 324) * mm});
            skLineSegment(sketch, "E517", {"start": v(882, 342) * mm, "end": v(900, 342) * mm});
            skLineSegment(sketch, "E518.trimOffspring", {"start": v(882, 342) * mm, "end": v(882, 360) * mm});
            skLineSegment(sketch, "E519.trimOffspring", {"start": v(900, 306) * mm, "end": v(900, 288) * mm});
            skLineSegment(sketch, "E520.trimOffspring", {"start": v(882, 306) * mm, "end": v(882, 324) * mm});
            skLineSegment(sketch, "E521.trimOffspring", {"start": v(900, 270) * mm, "end": v(900, 252) * mm});
            skLineSegment(sketch, "E522.trimOffspring", {"start": v(882, 270) * mm, "end": v(882, 288) * mm});
            skLineSegment(sketch, "E523.trimOffspring", {"start": v(900, 234) * mm, "end": v(900, 216) * mm});
            skLineSegment(sketch, "E524.trimOffspring", {"start": v(900, 126) * mm, "end": v(900, 108) * mm});
            skLineSegment(sketch, "E525.trimOffspring", {"start": v(882, 162) * mm, "end": v(882, 180) * mm});
            skLineSegment(sketch, "E526.trimOffspring", {"start": v(900, 162) * mm, "end": v(900, 144) * mm});
            skLineSegment(sketch, "E527.trimOffspring", {"start": v(882, 198) * mm, "end": v(882, 216) * mm});
            skLineSegment(sketch, "E528.trimOffspring", {"start": v(900, 198) * mm, "end": v(900, 180) * mm});
            skLineSegment(sketch, "E529.trimOffspring", {"start": v(882, 234) * mm, "end": v(882, 252) * mm});
            skLineSegment(sketch, "E530", {"start": v(1482, 360) * mm, "end": v(1482, 342) * mm});
            skLineSegment(sketch, "E531", {"start": v(1482, 126) * mm, "end": v(1500, 126) * mm});
            skLineSegment(sketch, "E532", {"start": v(1482, 144) * mm, "end": v(1500, 144) * mm});
            skLineSegment(sketch, "E533", {"start": v(1482, 162) * mm, "end": v(1500, 162) * mm});
            skLineSegment(sketch, "E534", {"start": v(1482, 180) * mm, "end": v(1500, 180) * mm});
            skLineSegment(sketch, "E535", {"start": v(1482, 198) * mm, "end": v(1500, 198) * mm});
            skLineSegment(sketch, "E536", {"start": v(1482, 216) * mm, "end": v(1500, 216) * mm});
            skLineSegment(sketch, "E537", {"start": v(1482, 234) * mm, "end": v(1500, 234) * mm});
            skLineSegment(sketch, "E538", {"start": v(1482, 252) * mm, "end": v(1500, 252) * mm});
            skLineSegment(sketch, "E539", {"start": v(1482, 270) * mm, "end": v(1500, 270) * mm});
            skLineSegment(sketch, "E540", {"start": v(1482, 306) * mm, "end": v(1500, 306) * mm});
            skLineSegment(sketch, "E541", {"start": v(1482, 324) * mm, "end": v(1500, 324) * mm});
            skLineSegment(sketch, "E542", {"start": v(1482, 342) * mm, "end": v(1500, 342) * mm});
            skLineSegment(sketch, "E543", {"start": v(1482, 288) * mm, "end": v(1500, 288) * mm});
            skLineSegment(sketch, "E544.trimOffspring", {"start": v(1500, 126) * mm, "end": v(1500, 108) * mm});
            skLineSegment(sketch, "E545.trimOffspring", {"start": v(1482, 144) * mm, "end": v(1482, 126) * mm});
            skLineSegment(sketch, "E546.trimOffspring", {"start": v(1500, 162) * mm, "end": v(1500, 144) * mm});
            skLineSegment(sketch, "E547.trimOffspring", {"start": v(1482, 180) * mm, "end": v(1482, 162) * mm});
            skLineSegment(sketch, "E548.trimOffspring", {"start": v(1500, 198) * mm, "end": v(1500, 180) * mm});
            skLineSegment(sketch, "E549.trimOffspring", {"start": v(1482, 216) * mm, "end": v(1482, 198) * mm});
            skLineSegment(sketch, "E550.trimOffspring", {"start": v(1500, 234) * mm, "end": v(1500, 216) * mm});
            skLineSegment(sketch, "E551.trimOffspring", {"start": v(1482, 252) * mm, "end": v(1482, 234) * mm});
            skLineSegment(sketch, "E552.trimOffspring", {"start": v(1500, 270) * mm, "end": v(1500, 252) * mm});
            skLineSegment(sketch, "E553.trimOffspring", {"start": v(1482, 288) * mm, "end": v(1482, 270) * mm});
            skLineSegment(sketch, "E554.trimOffspring", {"start": v(1500, 306) * mm, "end": v(1500, 288) * mm});
            skLineSegment(sketch, "E555.trimOffspring", {"start": v(1482, 324) * mm, "end": v(1482, 306) * mm});
            skSolve(sketch);
        }
        {
            var Q0;
            Q0 = qSketchRegion(id + "F20", true);
            extrude(context, id + "F21", {"entities" : qUnion([Q0]), "depth" : 18 * mm});
        }
        {
            var Q0;
            Q0=qCreatedBy(makeId("Front.planeOp"),FACE);
            var sketch = newSketch(context, id + "F22", { "sketchPlane" : qUnion([Q0])});
            skLineSegment(sketch, "E556", {"start": v(18, 43) * mm, "end": v(18, 143) * mm});
            skLineSegment(sketch, "E557", {"start": v(18, 143) * mm, "end": v(48, 143) * mm});
            skLineSegment(sketch, "E558", {"start": v(48, 143) * mm, "end": v(48, 83) * mm});
            skLineSegment(sketch, "E559", {"start": v(83, 48) * mm, "end": v(143, 48) * mm});
            skLineSegment(sketch, "E560", {"start": v(143, 48) * mm, "end": v(143, 18) * mm});
            skLineSegment(sketch, "E561", {"start": v(143, 18) * mm, "end": v(43, 18) * mm});
            skLineSegment(sketch, "E562", {"start": v(43, 18) * mm, "end": v(18, 43) * mm});
            skLineSegment(sketch, "E563", {"start": v(48, 83) * mm, "end": v(83, 83) * mm});
            skLineSegment(sketch, "E564", {"start": v(83, 83) * mm, "end": v(83, 48) * mm});
            skCircle(sketch, "E565", {"center": v(48, 48) * mm, "radius": 12.5 * mm});
            skLineSegment(sketch, "E566", {"start": v(0, 0) * mm, "end": v(83, 83) * mm, "construction": true});
            skSolve(sketch);
        }
        {
            var Q0;
            Q0 = qSketchRegion(id + "F22", true);
            extrude(context, id + "F23", {"entities" : qUnion([Q0]), "oppositeDirection" : true, "depth" : 18 * mm});
        }
    });
